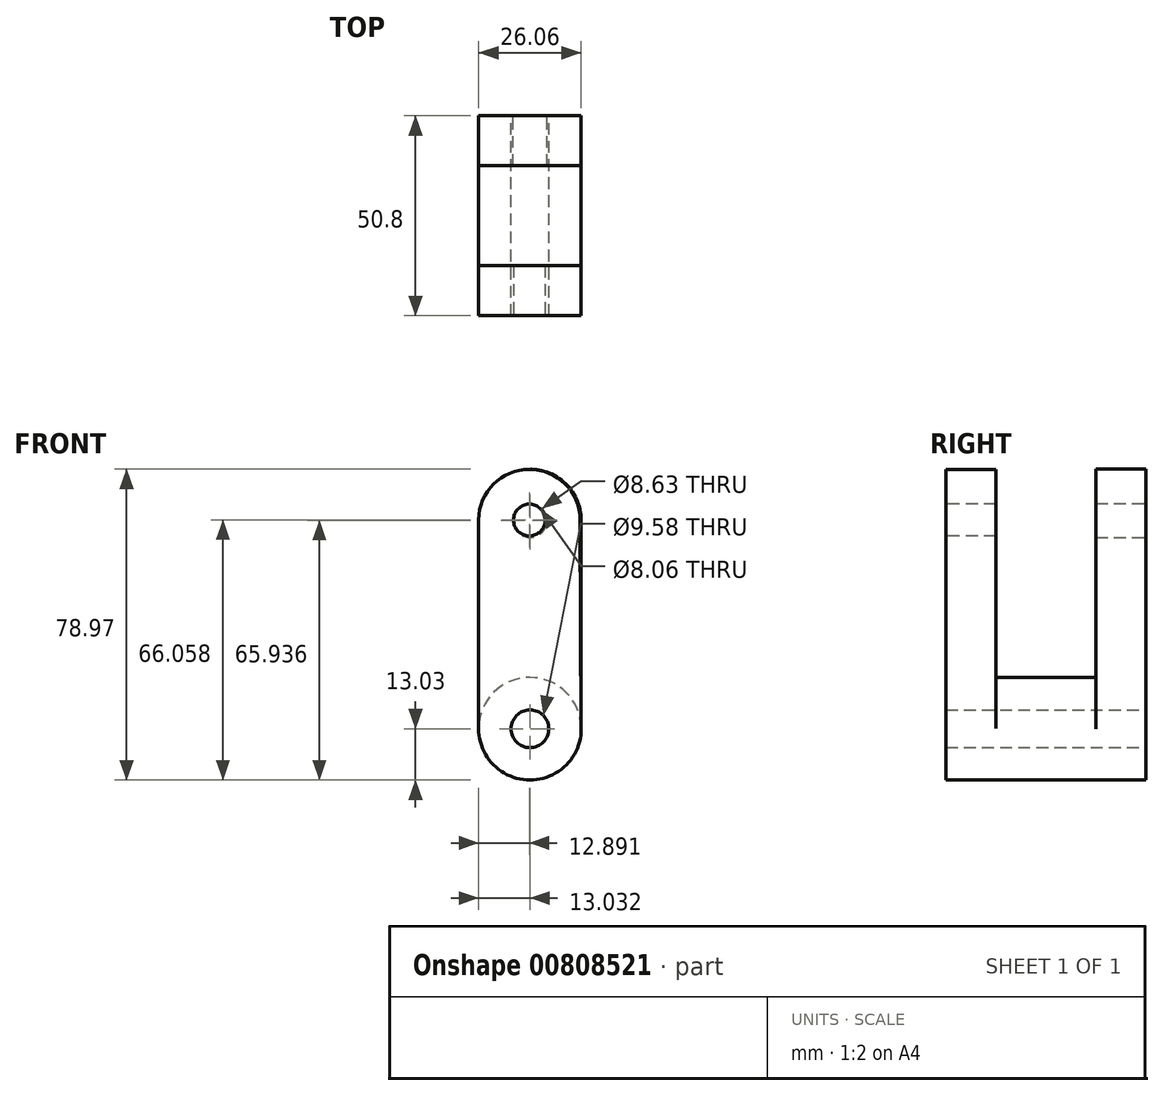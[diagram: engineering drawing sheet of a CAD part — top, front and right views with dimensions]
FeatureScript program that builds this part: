
annotation { "Feature Type Name" : "Feature", "Feature Type Description" : "" }
export const myFeature = defineFeature(function(context is Context, id is Id, definition is map)
    precondition{}
    {
        {
            var Q0;
            Q0=qCreatedBy(makeId("Front.planeOp"),FACE);
            var sketch = newSketch(context, id + "F0", { "sketchPlane" : qUnion([Q0])});
            skLineSegment(sketch, "E0.left", {"start": v(-16.55, 31.93) * mm, "end": v(-16.55, -20.98) * mm});
            skLineSegment(sketch, "E0.right", {"start": v(9.51, 31.93) * mm, "end": v(9.51, -20.98) * mm});
            skArc(sketch, "E1", {"start": v(9.51, 31.93) * mm, "mid": v(-3.52, 44.96) * mm, "end": v(-16.55, 31.93) * mm});
            skArc(sketch, "E2", {"start": v(-16.55, -20.98) * mm, "mid": v(-3.52, -34.01) * mm, "end": v(9.51, -20.98) * mm});
            skCircle(sketch, "E3", {"center": v(-3.52, 31.93) * mm, "radius": 4.31 * mm});
            skCircle(sketch, "E4", {"center": v(-3.52, -20.98) * mm, "radius": 4.8 * mm});
            skCircle(sketch, "E5", {"center": v(-3.52, -20.98) * mm, "radius": 13.03 * mm});
            skSolve(sketch);
        }
        {
            var Q0;
            Q0 = qSketchRegion(id + "F0", true);
            extrude(context, id + "F1", {"entities" : qUnion([Q0]), "depth" : 12.7 * mm, "offsetDistance" : 25.4 * mm});
        }
        {
            var Q0;
            Q0=makeQuery(id+"F0.imprint","IMPRINT",FACE,{"disambiguationData":[TD([[makeQuery(id+"F0.imprint","IMPRINT",EDGE,{"derivedFrom":sQuery(id+"F0.wireOp",EDGE,"E4")}),-1.0]])]});
            var Q1;
            Q1 = qSketchRegion(id + "FMDru2Qpxw92j5B_1", true);
            extrude(context, id + "F2", {"entities" : qUnion([Q0, Q1]), "operationType" : NewBodyOperationType.ADD, "depth" : 50.8 * mm, "offsetDistance" : 25.4 * mm});
        }
        {
            var Q0;
            Q0=makeQuery(id+"F2.opExtrude","CAP_FACE",FACE,{"disambiguationData":[OSD([sQuery(id+"F0.wireOp",EDGE,"E4"),sQuery(id+"F0.wireOp",EDGE,"E5")])],"isStart":false});
            var sketch = newSketch(context, id + "F3", { "sketchPlane" : qUnion([Q0])});
            skLineSegment(sketch, "E6", {"start": v(-16.55, -21.05) * mm, "end": v(-16.55, 32.12) * mm});
            skLineSegment(sketch, "E7", {"start": v(9.23, 32.12) * mm, "end": v(9.51, -20.91) * mm});
            skArc(sketch, "E8", {"start": v(9.23, 32.12) * mm, "mid": v(-3.66, 44.94) * mm, "end": v(-16.55, 32.12) * mm});
            skCircle(sketch, "E9", {"center": v(-3.66, 32.05) * mm, "radius": 4.4 * mm});
            skSolve(sketch);
        }
        {
            var Q0;
            Q0 = qSketchRegion(id + "F3", true);
            var Q1;
            {var subQ1=sQuery(id+"F3.wireOp",EDGE,"E7");Q1=makeQuery(id+"F3.imprint","IMPRINT",FACE,{"disambiguationData":[TD([[makeQuery(id+"F3.imprint","IMPRINT",EDGE,{"derivedFrom":subQ1}),-1.0]])]});}
            extrude(context, id + "F4", {"entities" : qUnion([Q0, Q1]), "operationType" : NewBodyOperationType.ADD, "oppositeDirection" : true, "depth" : 12.7 * mm, "offsetDistance" : 25.4 * mm});
        }
        {
            var Q0;
            {var subQ0=sQuery(id+"F0.wireOp",EDGE,"E5");Q0=makeQuery(id+"F4.boolean.opBoolean","MERGE",FACE,{"derivedFrom":[makeQuery(id+"F2.opExtrude","CAP_FACE",FACE,{"disambiguationData":[OSD([sQuery(id+"F0.wireOp",EDGE,"E4"),subQ0])],"isStart":false}),makeQuery(id+"F4.opExtrude","CAP_FACE",FACE,{"disambiguationData":[OSD([subQ0,sQuery(id+"F3.wireOp",EDGE,"E6"),sQuery(id+"F3.wireOp",EDGE,"E7"),sQuery(id+"F3.wireOp",EDGE,"E8")])],"isStart":true})]});}
            var sketch = newSketch(context, id + "F5", { "sketchPlane" : qUnion([Q0])});
            skCircle(sketch, "E10", {"center": v(-3.66, 32.05) * mm, "radius": 4.03 * mm});
            skSolve(sketch);
        }
        {
            var Q0;
            Q0=makeQuery(id+"F5.imprint","IMPRINT",FACE,{"disambiguationData":[TD([[makeQuery(id+"F5.imprint","IMPRINT",EDGE,{"derivedFrom":sQuery(id+"F5.wireOp",EDGE,"E10")}),1.0]])]});
            extrude(context, id + "F6", {"entities" : qUnion([Q0]), "operationType" : NewBodyOperationType.REMOVE, "oppositeDirection" : true, "depth" : 25.4 * mm, "offsetDistance" : 25.4 * mm});
        }
    });
